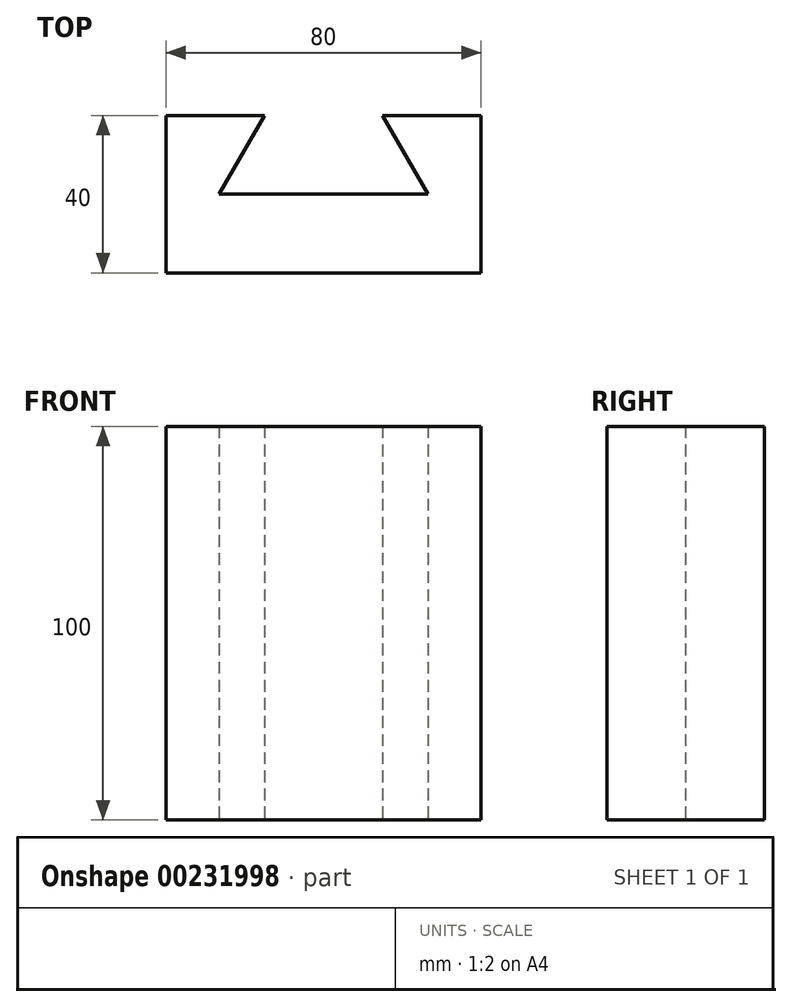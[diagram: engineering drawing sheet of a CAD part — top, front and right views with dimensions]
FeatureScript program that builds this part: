
annotation { "Feature Type Name" : "Feature", "Feature Type Description" : "" }
export const myFeature = defineFeature(function(context is Context, id is Id, definition is map)
    precondition{}
    {
        {
            var Q0;
            Q0=qCreatedBy(makeId("Top.planeOp"),FACE);
            var sketch = newSketch(context, id + "F0", { "sketchPlane" : qUnion([Q0])});
            skLineSegment(sketch, "E0", {"start": v(0, 0) * mm, "end": v(-40, 0) * mm});
            skLineSegment(sketch, "E1", {"start": v(-40, 0) * mm, "end": v(-40, 40) * mm});
            skLineSegment(sketch, "E2", {"start": v(-40, 40) * mm, "end": v(-15, 40) * mm});
            skLineSegment(sketch, "E3", {"start": v(-15, 40) * mm, "end": v(-26.55, 20) * mm});
            skLineSegment(sketch, "E4", {"start": v(-26.55, 20) * mm, "end": v(0, 20) * mm});
            skLineSegment(sketch, "E5.MirrorCS", {"start": v(0, 0) * mm, "end": v(40, 0) * mm});
            skLineSegment(sketch, "E6.MirrorCS", {"start": v(40, 40) * mm, "end": v(15, 40) * mm});
            skLineSegment(sketch, "E7.MirrorCS", {"start": v(26.55, 20) * mm, "end": v(0, 20) * mm});
            skLineSegment(sketch, "E8.MirrorCS", {"start": v(40, 0) * mm, "end": v(40, 40) * mm});
            skLineSegment(sketch, "E9.MirrorCS", {"start": v(15, 40) * mm, "end": v(26.55, 20) * mm});
            skSolve(sketch);
        }
        {
            var Q0;
            Q0=makeQuery(id+"F0.imprint","IMPRINT",FACE,{"disambiguationData":[TD([[makeQuery(id+"F0.imprint","IMPRINT",EDGE,{"derivedFrom":sQuery(id+"F0.wireOp",EDGE,"E0")}),-1.0]])]});
            extrude(context, id + "F1", {"entities" : qUnion([Q0]), "depth" : 100 * mm});
        }
    });
